# Revit family: okamura_Drape_Tri_Panel 1920H Tabletop 1000H Left
name_source: partatom
category: Furniture
revit_build: Autodesk Revit 2017 (Build: 20160225_1515(x64)
units: mm (PartAtom-declared; Revit-internal decimal feet)

## family parameters
Always vertical = Yes
Cut with Voids When Loaded = No
OmniClass Number = 23.40.20.00
OmniClass Title = General Furniture and Specialties
Room Calculation Point = No
Shared = No
Work Plane-Based = No

## types (72) — shared parameters
Assembly Code = E2020200
Bracket & Leveler = okm_ZK25
D = 1000 mm  [stored 3.28084 ft]
H = 1920 mm  [stored 6.29921 ft]
Keynote = 12490
Kind = Booth
Manufacturer = Okamura Corporation
Power = okm_Y707
Product Categories = Desks and Workspaces
Product Number = *
Verticle Wiring Duct = okm_Z606
W = 1000 mm  [stored 3.28084 ft]
Wire management tray = okm_Z606

## per-type parameters (varying)
| type | Inner panel | Outer panel | Tabletop | URL | Wall Light |
| FLZ0(Beige/Light gray) & MHE6(White/Black) | okm_FJY2 | okm_FJY1 | okm_MG99 | http://www.okamura.co.jp | okm_ZA75 |
| FLZ1(Dark brown/Light gray) & MHE6(White/Black) | okm_FJY2 | okm_FJY1 | okm_MG99 | http://www.okamura.co.jp | okm_ZA75 |
| FLZ3(Gray/Light gray) & MHE6(White/Black) | okm_FJY2 | okm_FJY3 | okm_MG99 | http://www.okamura.co.jp | okm_ZA75 |
| FLZ4(Dark gray/Light gray) & MHE6(White/Black) | okm_FJY2 | okm_FJY4 | okm_MG99 | http://www.okamura.co.jp | okm_ZA75 |
| FLZ5(Indigo/Light gray) & MHE6(White/Black) | okm_FJY2 | okm_FJY5 | okm_MG99 | http://www.okamura.co.jp | okm_ZA75 |
| FLZ6(Sage/Light gray) & MHE6(White/Black) | okm_FJY2 | okm_FJY6 | okm_MG99 | http://www.okamura.co.jp | okm_ZA75 |
| FLZ7(Green/Light gray) & MHE6(White/Black) | okm_FJY2 | okm_FJY7 | okm_MG99 | http://www.okamura.co.jp | okm_ZA75 |
| FLZ8(Yellow /Light gray) & MHE6(White/Black) | okm_FJY2 | okm_FJY8 | okm_MG99 | http://www.okamura.com | okm_ZA75 |
| FLZ9(Orange red/Light gray) & MHE6(White/Black) | okm_FJY2 | okm_FJY9 | okm_MG99 | http://www.okamura.co.jp | okm_MG99 |
| FNV0(Dark gray/Beige) & MHE6(White/Black) | okm_FXT2 | okm_FXT0 | okm_MG99 | http://www.okamura.co.jp | okm_ZA75 |
| FNV1(Gray/Beige) & MHE6(White/Black) | okm_FXT2 | okm_FXT1 | okm_MG99 | http://www.okamura.co.jp | okm_ZA75 |
| FNV3(Dark brown/Beige) & MHE6(White/Black) | okm_FXT2 | okm_FXT3 | okm_MG99 | http://www.okamura.co.jp | okm_ZA75 |
| FNV4(Indigo/Beige) & MHE6(White/Black) | okm_FXT2 | okm_FXT4 | okm_MG99 | http://www.okamura.co.jp | okm_ZA75 |
| FNV5(Dark green/Beige) & MHE6(White/Black) | okm_FXT2 | okm_FXT5 | okm_MG99 | http://www.okamura.co.jp | okm_ZA75 |
| FNV6(Terracotta/Beige) & MHE6(White/Black) | okm_FXT2 | okm_FXT6 | okm_MG99 | http://www.okamura.co.jp | okm_ZA75 |
| FNV7(Yellow/Beige) & MHE6(White/Black) | okm_FXT2 | okm_FXT7 | okm_MG99 | http://www.okamura.co.jp | okm_ZA75 |
| FNV8(Pale pink/Beige) & MHE6(White/Black) | okm_FXT2 | okm_FXT8 | okm_MG99 | http://www.okamura.co.jp | okm_ZA75 |
| FNV9(Sage/Beige) & MHE6(White/Black) | okm_FXT2 | okm_FXT9 | okm_MG99 | http://www.okamura.co.jp | okm_ZA75 |
| FLZ0(Beige/Light gray) & MHV3(Prize Wood Light/Black) | okm_FJY2 | okm_FJY1 | okm_MX61 | http://www.okamura.co.jp | okm_ZA75 |
| FLZ1(Dark brown/Light gray) & MHV3(Prize Wood Light/Black) | okm_FJY2 | okm_FJY1 | okm_MX61 | http://www.okamura.co.jp | okm_ZA75 |
| FLZ3(Gray/Light gray) & MHV3(Prize Wood Light/Black) | okm_FJY2 | okm_FJY3 | okm_MX61 | http://www.okamura.co.jp | okm_ZA75 |
| FLZ4(Dark gray/Light gray) & MHV3(Prize Wood Light/Black) | okm_FJY2 | okm_FJY4 | okm_MX61 | http://www.okamura.co.jp | okm_ZA75 |
| FLZ5(Indigo/Light gray) & MHV3(Prize Wood Light/Black) | okm_FJY2 | okm_FJY5 | okm_MX61 | http://www.okamura.co.jp | okm_ZA75 |
| FLZ6(Sage/Light gray) & MHV3(Prize Wood Light/Black) | okm_FJY2 | okm_FJY6 | okm_MX61 | http://www.okamura.co.jp | okm_ZA75 |
| FLZ7(Green/Light gray) & MHV3(Prize Wood Light/Black) | okm_FJY2 | okm_FJY7 | okm_MX61 | http://www.okamura.co.jp | okm_ZA75 |
| FLZ8(Yellow /Light gray) & MHV3(Prize Wood Light/Black) | okm_FJY2 | okm_FJY8 | okm_MX61 | http://www.okamura.com | okm_ZA75 |
| FLZ9(Orange red/Light gray) & MHV3(Prize Wood Light/Black) | okm_FJY2 | okm_FJY9 | okm_MX61 | http://www.okamura.co.jp | okm_MG99 |
| FNV0(Dark gray/Beige) & MHV3(Prize Wood Light/Black) | okm_FXT2 | okm_FXT0 | okm_MX61 | http://www.okamura.co.jp | okm_ZA75 |
| FNV1(Gray/Beige) & MHV3(Prize Wood Light/Black) | okm_FXT2 | okm_FXT1 | okm_MX61 | http://www.okamura.co.jp | okm_ZA75 |
| FNV3(Dark brown/Beige) & MHV3(Prize Wood Light/Black) | okm_FXT2 | okm_FXT3 | okm_MX61 | http://www.okamura.co.jp | okm_ZA75 |
| FNV4(Indigo/Beige) & MHV3(Prize Wood Light/Black) | okm_FXT2 | okm_FXT4 | okm_MX61 | http://www.okamura.co.jp | okm_ZA75 |
| FNV5(Dark green/Beige) & MHV3(Prize Wood Light/Black) | okm_FXT2 | okm_FXT5 | okm_MX61 | http://www.okamura.co.jp | okm_ZA75 |
| FNV6(Terracotta/Beige) & MHV3(Prize Wood Light/Black) | okm_FXT2 | okm_FXT6 | okm_MX61 | http://www.okamura.co.jp | okm_ZA75 |
| FNV7(Yellow/Beige) & MHV3(Prize Wood Light/Black) | okm_FXT2 | okm_FXT7 | okm_MX61 | http://www.okamura.co.jp | okm_ZA75 |
| FNV8(Pale pink/Beige) & MHV3(Prize Wood Light/Black) | okm_FXT2 | okm_FXT8 | okm_MX61 | http://www.okamura.co.jp | okm_ZA75 |
| FNV9(Sage/Beige) & MHV3(Prize Wood Light/Black) | okm_FXT2 | okm_FXT9 | okm_MX61 | http://www.okamura.co.jp | okm_ZA75 |
| FLZ4(Dark gray/Light gray) & MHV4(Prize Wood Medium/Black) | okm_FJY2 | okm_FJY4 | okm_MX62 | http://www.okamura.co.jp | okm_ZA75 |
| FLZ4(Dark gray/Light gray) & MHV5(Prize Wood Dark/Black) | okm_FJY2 | okm_FJY4 | okm_MX63 | http://www.okamura.co.jp | okm_ZA75 |
| FLZ0(Beige/Light gray) & MHV4(Prize Wood Medium/Black) | okm_FJY2 | okm_FJY1 | okm_MX62 | http://www.okamura.co.jp | okm_ZA75 |
| FLZ0(Beige/Light gray) & MHV5(Prize Wood Dark/Black) | okm_FJY2 | okm_FJY1 | okm_MX63 | http://www.okamura.co.jp | okm_ZA75 |
| FLZ1(Dark brown/Light gray) & MHV4(Prize Wood Medium/Black) | okm_FJY2 | okm_FJY1 | okm_MX62 | http://www.okamura.co.jp | okm_ZA75 |
| FLZ1(Dark brown/Light gray) & MHV5(Prize Wood Dark/Black) | okm_FJY2 | okm_FJY1 | okm_MX63 | http://www.okamura.co.jp | okm_ZA75 |
| FLZ3(Gray/Light gray) & MHV4(Prize Wood Medium/Black) | okm_FJY2 | okm_FJY3 | okm_MX62 | http://www.okamura.co.jp | okm_ZA75 |
| FLZ3(Gray/Light gray) & MHV5(Prize Wood Dark/Black) | okm_FJY2 | okm_FJY3 | okm_MX63 | http://www.okamura.co.jp | okm_ZA75 |
| FLZ5(Indigo/Light gray) & MHV4(Prize Wood Medium/Black) | okm_FJY2 | okm_FJY5 | okm_MX62 | http://www.okamura.co.jp | okm_ZA75 |
| FLZ5(Indigo/Light gray) & MHV5(Prize Wood Dark/Black) | okm_FJY2 | okm_FJY5 | okm_MX63 | http://www.okamura.co.jp | okm_ZA75 |
| FLZ6(Sage/Light gray) & MHV3(Prize Wood Medium/Black) | okm_FJY2 | okm_FJY6 | okm_MX62 | http://www.okamura.co.jp | okm_ZA75 |
| FLZ6(Sage/Light gray) & MHV5(Prize Wood Dark/Black) | okm_FJY2 | okm_FJY6 | okm_MX63 | http://www.okamura.co.jp | okm_ZA75 |
| FLZ7(Green/Light gray) & MHV4(Prize Wood Medium/Black) | okm_FJY2 | okm_FJY7 | okm_MX62 | http://www.okamura.co.jp | okm_ZA75 |
| FLZ7(Green/Light gray) & MHV5(Prize Wood Dark/Black) | okm_FJY2 | okm_FJY7 | okm_MX63 | http://www.okamura.co.jp | okm_ZA75 |
| FLZ8(Yellow /Light gray) & MHV4(Prize Wood Medium/Black) | okm_FJY2 | okm_FJY8 | okm_MX62 | http://www.okamura.com | okm_ZA75 |
| FLZ8(Yellow /Light gray) & MHV5(Prize Wood Dark/Black) | okm_FJY2 | okm_FJY8 | okm_MX63 | http://www.okamura.com | okm_ZA75 |
| FLZ9(Orange red/Light gray) & MHV4(Prize Wood Medium/Black) | okm_FJY2 | okm_FJY9 | okm_MX62 | http://www.okamura.co.jp | okm_MG99 |
| FLZ9(Orange red/Light gray) & MHV5(Prize Wood Dark/Black) | okm_FJY2 | okm_FJY9 | okm_MX63 | http://www.okamura.co.jp | okm_MG99 |
| FNV0(Dark gray/Beige) & MHV4(Prize Wood Medium/Black) | okm_FXT2 | okm_FXT0 | okm_MX62 | http://www.okamura.co.jp | okm_ZA75 |
| FNV0(Dark gray/Beige) & MHV5(Prize Wood Dark/Black) | okm_FXT2 | okm_FXT0 | okm_MX63 | http://www.okamura.co.jp | okm_ZA75 |
| FNV1(Gray/Beige) & MHV4(Prize Wood Medium/Black) | okm_FXT2 | okm_FXT1 | okm_MX62 | http://www.okamura.co.jp | okm_ZA75 |
| FNV1(Gray/Beige) & MHV5(Prize Wood Dark/Black) | okm_FXT2 | okm_FXT1 | okm_MX63 | http://www.okamura.co.jp | okm_ZA75 |
| FNV3(Dark brown/Beige) & MHV4(Prize Wood Medium/Black) | okm_FXT2 | okm_FXT3 | okm_MX62 | http://www.okamura.co.jp | okm_ZA75 |
| FNV3(Dark brown/Beige) & MHV5(Prize Wood Dark/Black) | okm_FXT2 | okm_FXT3 | okm_MX63 | http://www.okamura.co.jp | okm_ZA75 |
| FNV4(Indigo/Beige) & MHV4(Prize Wood Medium/Black) | okm_FXT2 | okm_FXT4 | okm_MX62 | http://www.okamura.co.jp | okm_ZA75 |
| FNV4(Indigo/Beige) & MHV5(Prize Wood Dark/Black) | okm_FXT2 | okm_FXT4 | okm_MX63 | http://www.okamura.co.jp | okm_ZA75 |
| FNV5(Dark green/Beige) & MHV4(Prize Wood Medium/Black) | okm_FXT2 | okm_FXT5 | okm_MX62 | http://www.okamura.co.jp | okm_ZA75 |
| FNV5(Dark green/Beige) & MHV5(Prize Wood Dark/Black) | okm_FXT2 | okm_FXT5 | okm_MX63 | http://www.okamura.co.jp | okm_ZA75 |
| FNV6(Terracotta/Beige) & MHV4(Prize Wood Medium/Black) | okm_FXT2 | okm_FXT6 | okm_MX62 | http://www.okamura.co.jp | okm_ZA75 |
| FNV6(Terracotta/Beige) & MHV5(Prize Wood Dark/Black) | okm_FXT2 | okm_FXT6 | okm_MX63 | http://www.okamura.co.jp | okm_ZA75 |
| FNV7(Yellow/Beige) & MHV4(Prize Wood Medium/Black) | okm_FXT2 | okm_FXT7 | okm_MX62 | http://www.okamura.co.jp | okm_ZA75 |
| FNV7(Yellow/Beige) & MHV5(Prize Wood Dark/Black) | okm_FXT2 | okm_FXT7 | okm_MX63 | http://www.okamura.co.jp | okm_ZA75 |
| FNV8(Pale pink/Beige) & MHV4(Prize Wood Medium/Black) | okm_FXT2 | okm_FXT8 | okm_MX62 | http://www.okamura.co.jp | okm_ZA75 |
| FNV8(Pale pink/Beige) & MHV5(Prize Wood Dark/Black) | okm_FXT2 | okm_FXT8 | okm_MX63 | http://www.okamura.co.jp | okm_ZA75 |
| FNV9(Sage/Beige) & MHV4(Prize Wood Medium/Black) | okm_FXT2 | okm_FXT9 | okm_MX62 | http://www.okamura.co.jp | okm_ZA75 |
| FNV9(Sage/Beige) & MHV5(Prize Wood Dark/Black) | okm_FXT2 | okm_FXT9 | okm_MX63 | http://www.okamura.co.jp | okm_ZA75 |

note: [stored X ft] marks values corroborated as IEEE doubles in the binary element streams (Revit-internal decimal feet)
